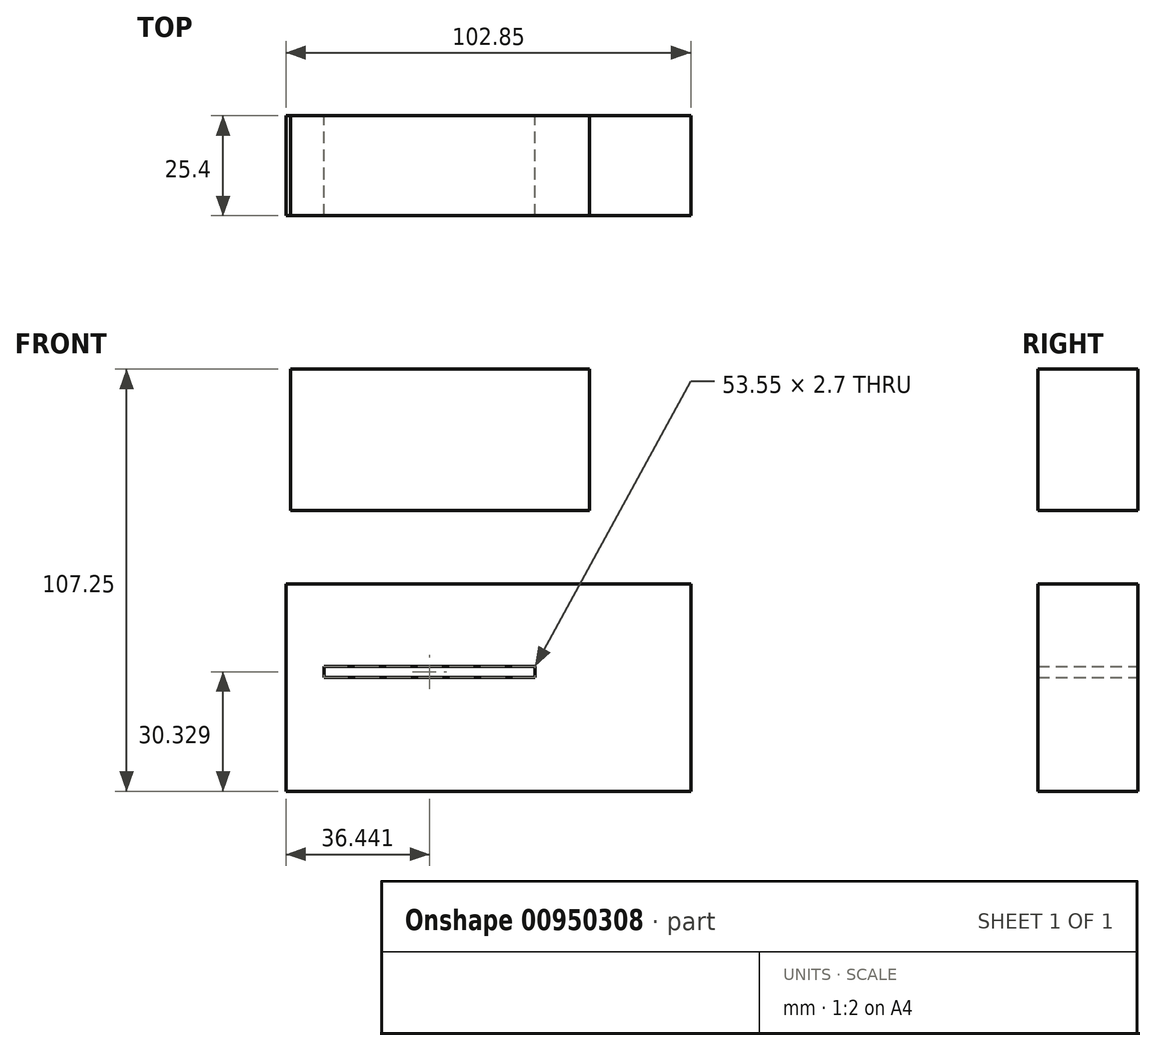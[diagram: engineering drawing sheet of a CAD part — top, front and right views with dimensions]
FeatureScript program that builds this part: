
annotation { "Feature Type Name" : "Feature", "Feature Type Description" : "" }
export const myFeature = defineFeature(function(context is Context, id is Id, definition is map)
    precondition{}
    {
        {
            var Q0;
            Q0=qCreatedBy(makeId("Front.planeOp"),FACE);
            var sketch = newSketch(context, id + "F0", { "sketchPlane" : qUnion([Q0])});
            skLineSegment(sketch, "E0.bottom", {"start": v(-46.65, 54.56) * mm, "end": v(29.35, 54.56) * mm});
            skLineSegment(sketch, "E0.top", {"start": v(-46.65, 18.62) * mm, "end": v(29.35, 18.62) * mm});
            skLineSegment(sketch, "E0.left", {"start": v(-46.65, 54.56) * mm, "end": v(-46.65, 18.62) * mm});
            skLineSegment(sketch, "E0.right", {"start": v(29.35, 54.56) * mm, "end": v(29.35, 18.62) * mm});
            skLineSegment(sketch, "E1.bottom", {"start": v(15.43, -21.01) * mm, "end": v(-38.13, -21.01) * mm});
            skLineSegment(sketch, "E1.top", {"start": v(15.43, -23.71) * mm, "end": v(-38.13, -23.71) * mm});
            skLineSegment(sketch, "E1.left", {"start": v(15.43, -21.01) * mm, "end": v(15.43, -23.71) * mm});
            skLineSegment(sketch, "E1.right", {"start": v(-38.13, -21.01) * mm, "end": v(-38.13, -23.71) * mm});
            skLineSegment(sketch, "E2.bottom", {"start": v(-47.79, -52.69) * mm, "end": v(55.06, -52.69) * mm});
            skLineSegment(sketch, "E2.top", {"start": v(-47.79, 0) * mm, "end": v(55.06, 0) * mm});
            skLineSegment(sketch, "E2.left", {"start": v(-47.79, -52.69) * mm, "end": v(-47.79, 0) * mm});
            skLineSegment(sketch, "E2.right", {"start": v(55.06, -52.69) * mm, "end": v(55.06, 0) * mm});
            skSolve(sketch);
        }
        {
            var Q0;
            Q0 = qSketchRegion(id + "F0", true);
            extrude(context, id + "F1", {"entities" : qUnion([Q0]), "depth" : 25.4 * mm, "offsetDistance" : 25.4 * mm});
        }
    });
